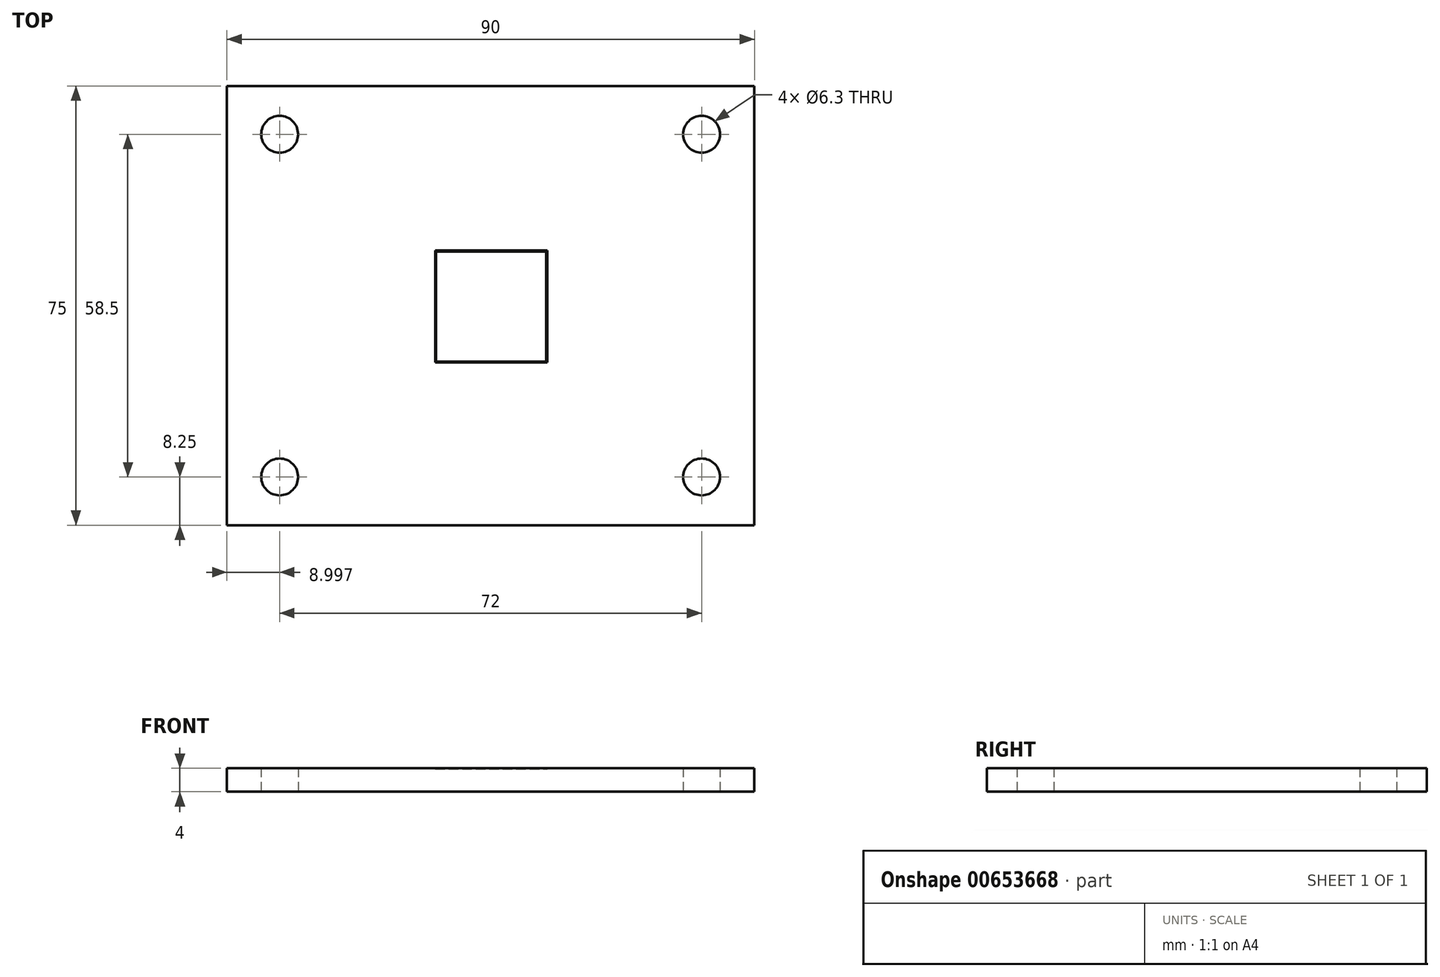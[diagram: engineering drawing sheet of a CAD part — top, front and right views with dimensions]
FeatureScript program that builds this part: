
annotation { "Feature Type Name" : "Feature", "Feature Type Description" : "" }
export const myFeature = defineFeature(function(context is Context, id is Id, definition is map)
    precondition{}
    {
        {
            var Q0;
            Q0=qCreatedBy(makeId("Top.planeOp"),FACE);
            var sketch = newSketch(context, id + "F0", { "sketchPlane" : qUnion([Q0])});
            skLineSegment(sketch, "E0.bottom", {"start": v(-46.6, 47.7) * mm, "end": v(43.4, 47.7) * mm});
            skLineSegment(sketch, "E0.top", {"start": v(-46.6, -27.3) * mm, "end": v(43.4, -27.3) * mm});
            skLineSegment(sketch, "E0.left", {"start": v(-46.6, 47.7) * mm, "end": v(-46.6, -27.3) * mm});
            skLineSegment(sketch, "E0.right", {"start": v(43.4, 47.7) * mm, "end": v(43.4, -27.3) * mm});
            skSolve(sketch);
        }
        {
            var Q0;
            Q0=makeQuery(id+"F0.imprint","IMPRINT",FACE,{"disambiguationData":[TD([[makeQuery(id+"F0.imprint","IMPRINT",EDGE,{"derivedFrom":sQuery(id+"F0.wireOp",EDGE,"E0.bottom")}),-1.0]])]});
            var sketch = newSketch(context, id + "F1", { "sketchPlane" : qUnion([Q0])});
            skCircle(sketch, "E1", {"center": v(-37.6, 39.44) * mm, "radius": 3.15 * mm});
            skCircle(sketch, "E2", {"center": v(34.4, 39.44) * mm, "radius": 3.15 * mm});
            skCircle(sketch, "E3", {"center": v(-37.6, -19.06) * mm, "radius": 3.15 * mm});
            skCircle(sketch, "E4", {"center": v(34.4, -19.06) * mm, "radius": 3.15 * mm});
            skSolve(sketch);
        }
        {
            var Q0;
            Q0=makeQuery(id+"F1.imprint","IMPRINT",FACE,{"disambiguationData":[TD([[makeQuery(id+"F1.imprint","IMPRINT",EDGE,{"derivedFrom":sQuery(id+"F1.wireOp",EDGE,"E1")}),-1.0]])]});
            extrude(context, id + "F2", {"entities" : qUnion([Q0]), "depth" : 4 * mm, "offsetDistance" : 25 * mm});
        }
        {
            var Q0;
            Q0=makeQuery(id+"F2.opExtrude","CAP_FACE",FACE,{"disambiguationData":[OSD([sQuery(id+"F0.wireOp",EDGE,"E0.bottom"),sQuery(id+"F0.wireOp",EDGE,"E0.top"),sQuery(id+"F0.wireOp",EDGE,"E0.left"),sQuery(id+"F0.wireOp",EDGE,"E0.right"),sQuery(id+"F1.wireOp",EDGE,"E1"),sQuery(id+"F1.wireOp",EDGE,"E2"),sQuery(id+"F1.wireOp",EDGE,"E3"),sQuery(id+"F1.wireOp",EDGE,"E4")])],"isStart":false});
            var sketch = newSketch(context, id + "F3", { "sketchPlane" : qUnion([Q0])});
            skLineSegment(sketch, "E5.bottom", {"start": v(-11.04, 19.6) * mm, "end": v(8.06, 19.6) * mm});
            skLineSegment(sketch, "E5.top", {"start": v(-11.04, 0.5) * mm, "end": v(8.06, 0.5) * mm});
            skLineSegment(sketch, "E5.left", {"start": v(-11.04, 19.6) * mm, "end": v(-11.04, 0.5) * mm});
            skLineSegment(sketch, "E5.right", {"start": v(8.06, 19.6) * mm, "end": v(8.06, 0.5) * mm});
            skSolve(sketch);
        }
        {
            var Q0;
            Q0=makeQuery(id+"F3.imprint","IMPRINT",FACE,{"disambiguationData":[TD([[makeQuery(id+"F3.imprint","IMPRINT",EDGE,{"derivedFrom":sQuery(id+"F3.wireOp",EDGE,"E5.bottom")}),-1.0]])]});
            var sketch = newSketch(context, id + "F4", { "sketchPlane" : qUnion([Q0])});
            skLineSegment(sketch, "E6.bottom", {"start": v(-11, 19.54) * mm, "end": v(8, 19.54) * mm});
            skLineSegment(sketch, "E6.top", {"start": v(-11, 0.54) * mm, "end": v(8, 0.54) * mm});
            skLineSegment(sketch, "E6.left", {"start": v(-11, 19.54) * mm, "end": v(-11, 0.54) * mm});
            skLineSegment(sketch, "E6.right", {"start": v(8, 19.54) * mm, "end": v(8, 0.54) * mm});
            skSolve(sketch);
        }
        {
            var Q0;
            Q0=makeQuery(id+"F3.imprint","IMPRINT",FACE,{"disambiguationData":[TD([[makeQuery(id+"F3.imprint","IMPRINT",EDGE,{"derivedFrom":sQuery(id+"F3.wireOp",EDGE,"E5.bottom")}),-1.0]])]});
            var Q1;
            Q1=makeQuery(id+"F4.imprint","IMPRINT",FACE,{"disambiguationData":[TD([[makeQuery(id+"F4.imprint","IMPRINT",EDGE,{"derivedFrom":sQuery(id+"F4.wireOp",EDGE,"E6.bottom")}),-1.0]])]});
            var Q2;
            Q2=makeQuery(id+"F4.imprint","IMPRINT",FACE,{"disambiguationData":[TD([[makeQuery(id+"F4.imprint","IMPRINT",EDGE,{"derivedFrom":sQuery(id+"F4.wireOp",EDGE,"E6.bottom")}),1.0]])]});
            extrude(context, id + "F5", {"entities" : qUnion([Q0, Q1, Q2]), "operationType" : NewBodyOperationType.REMOVE, "oppositeDirection" : true, "depth" : 0.1 * mm, "offsetDistance" : 25 * mm});
        }
        {
            var Q0;
            {var subQ0=sQuery(id+"F3.wireOp",EDGE,"E5.right");var subQ1=sQuery(id+"F3.wireOp",EDGE,"E5.left");var subQ2=sQuery(id+"F3.wireOp",EDGE,"E5.top");var subQ3=sQuery(id+"F3.wireOp",EDGE,"E5.bottom");Q0=makeQuery(id+"F5.boolean.opBoolean","COPY",FACE,{"derivedFrom":makeQuery(id+"F5.opExtrude","CAP_FACE",FACE,{"disambiguationData":[OSD([subQ3,subQ2,subQ1,subQ0]),TDD([makeQuery(id+"F3.imprint","IMPRINT",EDGE,{"derivedFrom":subQ3}),makeQuery(id+"F3.imprint","IMPRINT",EDGE,{"derivedFrom":subQ2}),makeQuery(id+"F3.imprint","IMPRINT",EDGE,{"derivedFrom":subQ1}),makeQuery(id+"F3.imprint","IMPRINT",EDGE,{"derivedFrom":subQ0})])],"isStart":false})});}
            var sketch = newSketch(context, id + "F6", { "sketchPlane" : qUnion([Q0])});
            skLineSegment(sketch, "E7.bottom", {"start": v(-10.9, 19.43) * mm, "end": v(7.9, 19.43) * mm});
            skLineSegment(sketch, "E7.top", {"start": v(-10.9, 0.63) * mm, "end": v(7.9, 0.63) * mm});
            skLineSegment(sketch, "E7.left", {"start": v(-10.9, 19.43) * mm, "end": v(-10.9, 0.63) * mm});
            skLineSegment(sketch, "E7.right", {"start": v(7.9, 19.43) * mm, "end": v(7.9, 0.63) * mm});
            skSolve(sketch);
        }
        {
            var Q0;
            Q0=makeQuery(id+"F6.imprint","IMPRINT",FACE,{"disambiguationData":[TD([[makeQuery(id+"F6.imprint","IMPRINT",EDGE,{"derivedFrom":sQuery(id+"F6.wireOp",EDGE,"E7.bottom")}),-1.0]])]});
            extrude(context, id + "F7", {"entities" : qUnion([Q0]), "operationType" : NewBodyOperationType.ADD, "depth" : 0.1 * mm, "offsetDistance" : 25 * mm});
        }
    });
